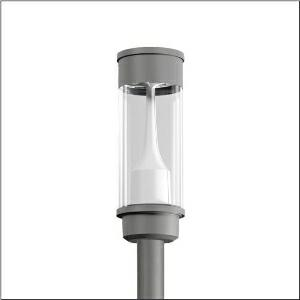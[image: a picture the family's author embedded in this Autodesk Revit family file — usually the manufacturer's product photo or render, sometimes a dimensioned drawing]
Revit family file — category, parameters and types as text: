
# Revit family: litepole_iq___pl1_2s_5xa5415jf14h_0c6a
name_source: partatom
category: Lighting Fixtures
units: mm (PartAtom-declared; Revit-internal decimal feet)

## family parameters
Cut with Voids When Loaded = No
Host = Face
Light Source = No
Part Type = Normal
Room Calculation Point = No
Round Connector Dimension = Use Diameter
Shared = No

## types (1)
- --- (1 x LED, 2970 lm, 19.3 W, 3000K)
    Apparent Load = 19 VA
    CIE Flux Codes = 23 62 94 96 100
    Color Rendering = 70
    Color Temperature = 3000K
    Default Elevation = 1800 mm
    Description = Litepole iQ, mast luminaire, Module 540 iQ-SR, primary light control with 3 zone facetted reflector, of plastic, silver coated, highly specular, structured, primary optical cover: cover, of PMMA, transparent, light distribution: PL1.2s, light emission: direct distribution, primary light characteristic: symmetric, installation type: post-top, LED, High Power LED, rated luminous flux: 2.970lm, luminous efficacy: 154lm/W, light colour: 730, colour temperature: 3000K, control gear: iQ Street-Remote, control: Auto-Match, Temp-Guard, Lumen-Switch, Night-Set, Smart-Wire, Light-Fading, Desk-Remote (wireless, voltage-free reading and setting of iQ features in the workshop via application-optimized NFC function/RFID function), optimised constant luminous flux control (CLO 2.0), Street-Remote, pre-setting: logarithmic dimming characteristic, with terminal, 6-pole, max. 2.5mm², mains connection: 230..240V, AC, 50/60Hz, start of lifetime: 19W, end of service life: 21W, reduction: 10W, luminaire housing, upper part, of glass-fibre reinforced polyester, coated, Siteco® metallic grey (DB 702S), diameter: 210mm, height: 590mm, spigot size: d x l = 76 x 70mm (post-top) | with reducer (optional accessory) 60 x 70mm, mounting height: 3..5m, post-top mast mounting element, of diecast aluminium, coated, Siteco® metallic grey (DB 702S), Module 540 iQ-SR, traffic white (RAL 9016), equipment: standard, protection rating (complete): IP65, insulation class (complete): insulation class II (safety insulation), certification: CE, ENEC, VDE, packaging unit: 1 piece

Light Distribution: PL1.2s
    Height = 590 mm
    Lamp = 1 x LED
    Lamp Light Flux = 2970 lm
    Lamp Power = 19.3 W
    Lamp count = 1
    Length = 220 mm
    Luminous efficacy = 154 lm/W
    Manufacturer = Siteco
    ModVariant = No
    Model = 5XA5415JF14H
    Number of Poles = 1
    OnlyDefault = Yes
    Power Factor = 1
    Product Name = Litepole iQ | PL1.2s
    Product group = mast luminaire | pylon top
    ProductGroupID = 6100
    Protection Class = Protection class II
    Protection Degree = IP 65
    RLX_Detail_Level = 1
    RLX_Emergency_Light_Flux = 0 lm
    RLX_Emergency_Type = 0
    RLX_Emergency_Type_DB = No
    RlxData = <blob elided: 24985 chars, md5=92790047>
    Socket = socket
    Standby Power = 0 W
    System Light Flux = 2970 lm
    System Power = 19 W
    Type Comments = factory setting: luminous flux: 100 % | dim-lin: 254 | 403 mA
    Type Image = l_1006025.jpg
    URL = http://relux.com
    VarID = @adj_144828
    Voltage = 0 V
    Weight = 0.00 kg
    Width = 0 mm  [stored 0 ft]

note: [stored X ft] marks values corroborated as IEEE doubles in the binary element streams (Revit-internal decimal feet)

## geometry (parser evidence)
native form markers: Blend x4, Sweep x10
no freeform markers — native parametric forms only
